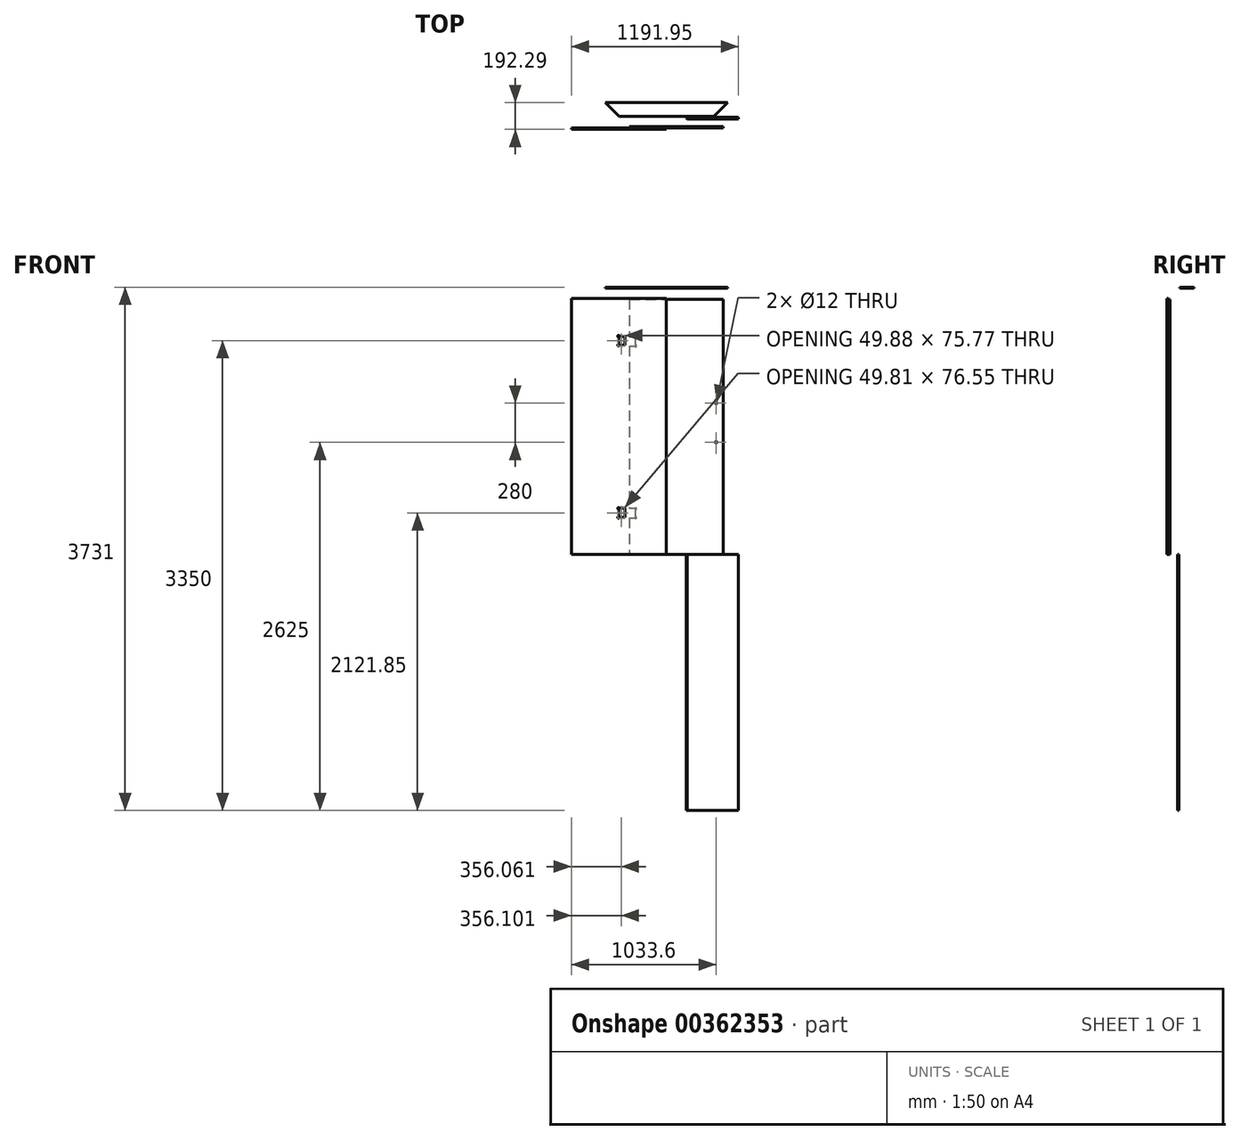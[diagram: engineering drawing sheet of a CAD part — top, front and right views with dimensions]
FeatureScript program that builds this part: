
annotation { "Feature Type Name" : "Feature", "Feature Type Description" : "" }
export const myFeature = defineFeature(function(context is Context, id is Id, definition is map)
    precondition{}
    {
        {
            var Q0;
            Q0=qCreatedBy(makeId("Top.planeOp"),FACE);
            var sketch = newSketch(context, id + "F0", { "sketchPlane" : qUnion([Q0])});
            skLineSegment(sketch, "E0.bottom", {"start": v(-342.07, -1.47) * mm, "end": v(335.93, -1.47) * mm});
            skLineSegment(sketch, "E0.top", {"start": v(-342.07, -11.47) * mm, "end": v(335.93, -11.47) * mm});
            skLineSegment(sketch, "E0.left", {"start": v(-342.07, -1.47) * mm, "end": v(-342.07, -11.47) * mm});
            skLineSegment(sketch, "E1", {"start": v(335.93, -1.47) * mm, "end": v(335.93, -11.47) * mm});
            skSolve(sketch);
        }
        {
            var Q0;
            Q0=makeQuery(id+"F0.imprint","IMPRINT",FACE,{"disambiguationData":[TD([[makeQuery(id+"F0.imprint","IMPRINT",EDGE,{"derivedFrom":sQuery(id+"F0.wireOp",EDGE,"E0.bottom")}),-1.0]])]});
            extrude(context, id + "F1", {"entities" : qUnion([Q0]), "depth" : 1825 * mm});
        }
        {
            var Q0;
            Q0=makeQuery(id+"F1.opExtrude","SWEPT_FACE",FACE,{"disambiguationData":[OSD([sQuery(id+"F0.wireOp",EDGE,"E0.top")])]});
            var sketch = newSketch(context, id + "F2", { "sketchPlane" : qUnion([Q0])});
            skLineSegment(sketch, "E2", {"start": v(38.93, 1557) * mm, "end": v(0.93, 1557) * mm});
            skLineSegment(sketch, "E3", {"start": v(-5.07, 1551) * mm, "end": v(-5.07, 1499) * mm});
            skLineSegment(sketch, "E4", {"start": v(0.93, 1493) * mm, "end": v(38.93, 1493) * mm});
            skLineSegment(sketch, "E5", {"start": v(38.93, 1493) * mm, "end": v(38.93, 1557) * mm});
            skArc(sketch, "E6", {"start": v(0.93, 1557) * mm, "mid": v(-9.3, 1561.24) * mm, "end": v(-5.07, 1551) * mm});
            skArc(sketch, "E7", {"start": v(-5.07, 1499) * mm, "mid": v(-9.3, 1488.76) * mm, "end": v(0.93, 1493) * mm});
            skLineSegment(sketch, "E8.0.1.0", {"start": v(38.93, 329.22) * mm, "end": v(1.1, 329.22) * mm});
            skLineSegment(sketch, "E8.0.1.1", {"start": v(-5.07, 323.23) * mm, "end": v(-5.07, 270.53) * mm});
            skLineSegment(sketch, "E8.0.1.2", {"start": v(0.91, 265.22) * mm, "end": v(38.93, 265.22) * mm});
            skLineSegment(sketch, "E8.0.1.3", {"start": v(38.93, 265.22) * mm, "end": v(38.93, 329.22) * mm});
            skArc(sketch, "E8.0.1.5", {"start": v(-5.07, 270.53) * mm, "mid": v(-9.03, 260.04) * mm, "end": v(0.91, 265.22) * mm});
            skPoint(sketch, "E9", {"position": v(-5.07, 1525) * mm});
            skPoint(sketch, "E10", {"position": v(-5.07, 300) * mm});
            skPoint(sketch, "E11", {"position": v(-90.95, 256.69) * mm});
            skArc(sketch, "E12", {"start": v(1.1, 329.22) * mm, "mid": v(-9.09, 333.52) * mm, "end": v(-5.07, 323.23) * mm});
            skPoint(sketch, "E13.orphan", {"position": v(-5.07, 329.47) * mm});
            skSolve(sketch);
        }
        {
            var Q0;
            {var subQ0=sQuery(id+"F2.wireOp",EDGE,"E5");Q0=makeQuery(id+"F2.imprint","IMPRINT",FACE,{"disambiguationData":[TD([[makeQuery(id+"F2.imprint","IMPRINT",EDGE,{"derivedFrom":subQ0}),1.0]])]});}
            var Q1;
            Q1=makeQuery(id+"F2.imprint","IMPRINT",FACE,{"disambiguationData":[TD([[makeQuery(id+"F2.imprint","IMPRINT",EDGE,{"derivedFrom":sQuery(id+"F2.wireOp",EDGE,"E3")}),1.0]])]});
            var Q2;
            Q2=makeQuery(id+"F2.imprint","IMPRINT",FACE,{"disambiguationData":[TD([[makeQuery(id+"F2.imprint","IMPRINT",EDGE,{"derivedFrom":sQuery(id+"F2.wireOp",EDGE,"E8.0.1.1")}),1.0]])]});
            var Q3;
            {var subQ0=sQuery(id+"F2.wireOp",EDGE,"E8.0.1.3");Q3=makeQuery(id+"F2.imprint","IMPRINT",FACE,{"disambiguationData":[TD([[makeQuery(id+"F2.imprint","IMPRINT",EDGE,{"derivedFrom":subQ0}),1.0]])]});}
            extrude(context, id + "F3", {"entities" : qUnion([Q0, Q1, Q2, Q3]), "operationType" : NewBodyOperationType.REMOVE, "endBound" : BoundingType.THROUGH_ALL, "oppositeDirection" : true, "depth" : 25 * mm});
        }
        {
            var Q0;
            Q0=qCreatedBy(makeId("Right.planeOp"),FACE);
            cPlane(context, id + "F4", {"entities" : qUnion([Q0]), "cplaneType" : CPlaneType.OFFSET, "offset" : 100 * mm, "width" : 150 * mm, "height" : 150 * mm});
        }
        {
            var Q0;
            Q0=qCreatedBy(makeId("Top.planeOp"),FACE);
            var sketch = newSketch(context, id + "F5", { "sketchPlane" : qUnion([Q0])});
            skLineSegment(sketch, "E14.bottom", {"start": v(119.88, 94.23) * mm, "end": v(492.88, 94.23) * mm});
            skLineSegment(sketch, "E14.top", {"start": v(119.88, 84.23) * mm, "end": v(484.88, 84.23) * mm});
            skLineSegment(sketch, "E14.left", {"start": v(119.88, 94.23) * mm, "end": v(119.88, 84.23) * mm});
            skLineSegment(sketch, "E15", {"start": v(484.88, 84.23) * mm, "end": v(492.88, 92.23) * mm});
            skLineSegment(sketch, "E16", {"start": v(492.88, 92.23) * mm, "end": v(492.88, 94.23) * mm});
            skSolve(sketch);
        }
        {
            var Q0;
            Q0=makeQuery(id+"F5.imprint","IMPRINT",FACE,{"disambiguationData":[TD([[makeQuery(id+"F5.imprint","IMPRINT",EDGE,{"derivedFrom":sQuery(id+"F5.wireOp",EDGE,"E14.bottom")}),-1.0]])]});
            extrude(context, id + "F6", {"entities" : qUnion([Q0]), "depth" : 1825 * mm});
        }
        {
            var Q0;
            Q0=makeQuery(id+"F6.opExtrude","SWEPT_BODY",BODY,{"disambiguationData":[OSD([sQuery(id+"F5.wireOp",EDGE,"E14.bottom"),sQuery(id+"F5.wireOp",EDGE,"E14.top"),sQuery(id+"F5.wireOp",EDGE,"E14.left"),sQuery(id+"F5.wireOp",EDGE,"E15"),sQuery(id+"F5.wireOp",EDGE,"E16")])]});
            var Q1;
            Q1=makeQuery(id+"F6.opExtrude","SWEPT_EDGE",EDGE,{"disambiguationData":[OSD([sQuery(id+"F5.wireOp",EDGE,"E14.top"),sQuery(id+"F5.wireOp",EDGE,"E15")])]});
            transform(context, id + "F7", {"entities" : qUnion([Q0]), "transformType" : TransformType.ROTATION, "transformAxis" : qUnion([Q1]), "angle" : 180 * degree, "makeCopy" : false});
        }
        {
            var Q0;
            Q0=makeQuery(id+"F6.opExtrude","SWEPT_BODY",BODY,{"disambiguationData":[OSD([sQuery(id+"F5.wireOp",EDGE,"E14.bottom"),sQuery(id+"F5.wireOp",EDGE,"E14.top"),sQuery(id+"F5.wireOp",EDGE,"E14.left"),sQuery(id+"F5.wireOp",EDGE,"E15"),sQuery(id+"F5.wireOp",EDGE,"E16")])]});
            var Q1;
            Q1=makeQuery(id+"F6.opExtrude","CAP_EDGE",EDGE,{"disambiguationData":[OSD([sQuery(id+"F5.wireOp",EDGE,"E14.bottom")])],"isStart":true});
            transform(context, id + "F8", {"entities" : qUnion([Q0]), "transformType" : TransformType.ROTATION, "transformAxis" : qUnion([Q1]), "angle" : 180 * degree, "makeCopy" : false});
        }
        {
            var Q0;
            Q0=makeQuery(id+"F1.opExtrude","SWEPT_BODY",BODY,{"disambiguationData":[OSD([sQuery(id+"F0.wireOp",EDGE,"E0.bottom"),sQuery(id+"F0.wireOp",EDGE,"E0.top"),sQuery(id+"F0.wireOp",EDGE,"E0.left"),sQuery(id+"F0.wireOp",EDGE,"j6zs9UJO-1aVY-m4L7-CDkp-rVGtMq2jGI5N"),sQuery(id+"F0.wireOp",EDGE,"xPVqqJFx-FA8w-VKuQ-6oFJ-jlqic1Wo0MHm")])]});
            var Q1;
            Q1=qCreatedBy(id+"F4.planeOp",FACE);
            transform(context, id + "F9", {"entities" : qUnion([Q0]), "transformType" : TransformType.TRANSLATION_DISTANCE, "transformDirection" : qUnion([Q1]), "distance" : 600 * mm, "makeCopy" : true});
        }
        {
            var Q0;
            Q0=makeQuery(id+"F9.opPattern","COPY",BODY,{"derivedFrom":makeQuery(id+"F1.opExtrude","SWEPT_BODY",BODY,{"disambiguationData":[OSD([sQuery(id+"F0.wireOp",EDGE,"E0.bottom"),sQuery(id+"F0.wireOp",EDGE,"E0.top"),sQuery(id+"F0.wireOp",EDGE,"E0.left"),sQuery(id+"F0.wireOp",EDGE,"j6zs9UJO-1aVY-m4L7-CDkp-rVGtMq2jGI5N"),sQuery(id+"F0.wireOp",EDGE,"xPVqqJFx-FA8w-VKuQ-6oFJ-jlqic1Wo0MHm")])]}),"instanceName":"1"});
            deleteBodies(context, id + "F10", {"entities" : qUnion([Q0])});
        }
        {
            var Q0;
            Q0=qCreatedBy(makeId("Top.planeOp"),FACE);
            var sketch = newSketch(context, id + "F11", { "sketchPlane" : qUnion([Q0])});
            skLineSegment(sketch, "E17.bottom", {"start": v(73.53, 0) * mm, "end": v(741.53, 0) * mm});
            skLineSegment(sketch, "E17.top", {"start": v(73.53, 10) * mm, "end": v(741.53, 10) * mm});
            skLineSegment(sketch, "E17.left", {"start": v(73.53, 0) * mm, "end": v(73.53, 10) * mm});
            skLineSegment(sketch, "E17.right", {"start": v(741.53, 0) * mm, "end": v(741.53, 10) * mm});
            skSolve(sketch);
        }
        {
            var Q0;
            Q0 = qSketchRegion(id + "F11", true);
            extrude(context, id + "F12", {"entities" : qUnion([Q0]), "depth" : 1820 * mm});
        }
        {
            var Q0;
            Q0=makeQuery(id+"F12.opExtrude","SWEPT_FACE",FACE,{"disambiguationData":[OSD([sQuery(id+"F11.wireOp",EDGE,"E17.bottom")])]});
            var sketch = newSketch(context, id + "F13", { "sketchPlane" : qUnion([Q0])});
            skLineSegment(sketch, "E18", {"start": v(138.9, 2778.57) * mm, "end": v(100.9, 2778.57) * mm});
            skLineSegment(sketch, "E19", {"start": v(94.9, 2772.57) * mm, "end": v(94.9, 2720.57) * mm});
            skLineSegment(sketch, "E20", {"start": v(100.9, 2714.57) * mm, "end": v(138.9, 2714.57) * mm});
            skLineSegment(sketch, "E21", {"start": v(138.9, 2714.57) * mm, "end": v(138.9, 2778.57) * mm});
            skArc(sketch, "E22", {"start": v(100.9, 2778.57) * mm, "mid": v(90.65, 2782.81) * mm, "end": v(94.9, 2772.57) * mm});
            skArc(sketch, "E23", {"start": v(94.9, 2720.57) * mm, "mid": v(90.65, 2710.33) * mm, "end": v(100.9, 2714.57) * mm});
            skLineSegment(sketch, "E24.0.1.0", {"start": v(111.53, 1550.8) * mm, "end": v(73.53, 1550.8) * mm});
            skLineSegment(sketch, "E24.0.1.1", {"start": v(73.53, 1550.8) * mm, "end": v(73.53, 1486.8) * mm});
            skLineSegment(sketch, "E24.0.1.2", {"start": v(73.53, 1486.8) * mm, "end": v(111.53, 1486.8) * mm});
            skLineSegment(sketch, "E24.0.1.3", {"start": v(117.53, 1492.8) * mm, "end": v(117.53, 1544.8) * mm});
            skPoint(sketch, "E25", {"position": v(94.9, 2746.57) * mm});
            skPoint(sketch, "E26", {"position": v(73.53, 1520) * mm});
            skPoint(sketch, "E27", {"position": v(9.01, 1478.26) * mm});
            skPoint(sketch, "E28.orphan", {"position": v(73.53, 1547.9) * mm});
            skPoint(sketch, "E29.orphan", {"position": v(73.53, 1492.1) * mm});
            skArc(sketch, "E30", {"start": v(117.53, 1544.8) * mm, "mid": v(121.77, 1555.04) * mm, "end": v(111.53, 1550.8) * mm});
            skArc(sketch, "E31", {"start": v(111.53, 1486.8) * mm, "mid": v(121.77, 1482.55) * mm, "end": v(117.53, 1492.8) * mm});
            skSolve(sketch);
        }
        {
            var Q0;
            {var subQ1=sQuery(id+"F13.wireOp",EDGE,"E24.0.1.0");Q0=makeQuery(id+"F13.imprint","IMPRINT",FACE,{"disambiguationData":[TD([[makeQuery(id+"F13.imprint","IMPRINT",EDGE,{"derivedFrom":subQ1}),-1.0]])]});}
            var sketch = newSketch(context, id + "F14", { "sketchPlane" : qUnion([Q0])});
            skLineSegment(sketch, "E32.0.1.0", {"start": v(111.53, 325.8) * mm, "end": v(73.53, 325.8) * mm});
            skLineSegment(sketch, "E32.0.1.1", {"start": v(73.53, 325.8) * mm, "end": v(73.53, 261.8) * mm});
            skLineSegment(sketch, "E32.0.1.2", {"start": v(73.53, 261.8) * mm, "end": v(111.53, 261.8) * mm});
            skLineSegment(sketch, "E32.0.1.3", {"start": v(117.53, 267.8) * mm, "end": v(117.53, 319.8) * mm});
            skPoint(sketch, "E33", {"position": v(119.88, 1526.81) * mm});
            skPoint(sketch, "E34", {"position": v(73.53, 295) * mm});
            skPoint(sketch, "E35", {"position": v(34, 258.5) * mm});
            skPoint(sketch, "E36.orphan", {"position": v(73.53, 322.9) * mm});
            skPoint(sketch, "E37.orphan", {"position": v(73.53, 267.1) * mm});
            skArc(sketch, "E38", {"start": v(117.53, 319.8) * mm, "mid": v(121.77, 330.04) * mm, "end": v(111.53, 325.8) * mm});
            skArc(sketch, "E39", {"start": v(111.53, 261.8) * mm, "mid": v(121.77, 257.55) * mm, "end": v(117.53, 267.8) * mm});
            skSolve(sketch);
        }
        {
            var Q0;
            Q0 = qSketchRegion(id + "F13", true);
            var Q1;
            Q1 = qSketchRegion(id + "F14", true);
            extrude(context, id + "F15", {"entities" : qUnion([Q0, Q1]), "operationType" : NewBodyOperationType.REMOVE, "endBound" : BoundingType.THROUGH_ALL, "oppositeDirection" : true, "depth" : 25 * mm});
        }
        {
            var Q0;
            Q0=makeQuery(id+"F12.opExtrude","SWEPT_FACE",FACE,{"disambiguationData":[OSD([sQuery(id+"F11.wireOp",EDGE,"E17.bottom")])]});
            var sketch = newSketch(context, id + "F16", { "sketchPlane" : qUnion([Q0])});
            skLineSegment(sketch, "E40.0", {"start": v(691.53, 1820) * mm, "end": v(691.53, 0) * mm, "construction": true});
            skLineSegment(sketch, "E41", {"start": v(797.67, 800) * mm, "end": v(449.98, 800) * mm, "construction": true});
            skLineSegment(sketch, "E42.0", {"start": v(797.67, 1080) * mm, "end": v(449.98, 1080) * mm, "construction": true});
            skCircle(sketch, "E43", {"center": v(691.53, 1080) * mm, "radius": 6 * mm});
            skCircle(sketch, "E44", {"center": v(691.53, 800) * mm, "radius": 6 * mm});
            skSolve(sketch);
        }
        {
            var Q0;
            Q0 = qSketchRegion(id + "F16", true);
            extrude(context, id + "F17", {"entities" : qUnion([Q0]), "operationType" : NewBodyOperationType.REMOVE, "endBound" : BoundingType.THROUGH_ALL, "oppositeDirection" : true, "depth" : 25 * mm});
        }
        {
            var Q0;
            Q0=qCreatedBy(makeId("Top.planeOp"),FACE);
            cPlane(context, id + "F18", {"entities" : qUnion([Q0]), "cplaneType" : CPlaneType.OFFSET, "offset" : 1900 * mm, "width" : 150 * mm, "height" : 150 * mm});
        }
        {
            var Q0;
            Q0=qCreatedBy(id+"F18.planeOp",FACE);
            var sketch = newSketch(context, id + "F19", { "sketchPlane" : qUnion([Q0])});
            skLineSegment(sketch, "E45", {"start": v(0, 80.82) * mm, "end": v(675, 80.82) * mm});
            skLineSegment(sketch, "E46.0", {"start": v(-100, 180.82) * mm, "end": v(775, 180.82) * mm});
            skLineSegment(sketch, "E47", {"start": v(675, 80.82) * mm, "end": v(775, 180.82) * mm});
            skLineSegment(sketch, "E48", {"start": v(0, 80.82) * mm, "end": v(-100, 180.82) * mm});
            skPoint(sketch, "E49.orphan", {"position": v(675, 180.82) * mm});
            skPoint(sketch, "E50.orphan", {"position": v(0, 180.82) * mm});
            skSolve(sketch);
        }
        {
            var Q0;
            Q0 = qSketchRegion(id + "F19", true);
            extrude(context, id + "F20", {"entities" : qUnion([Q0]), "depth" : 6 * mm});
        }
    });
